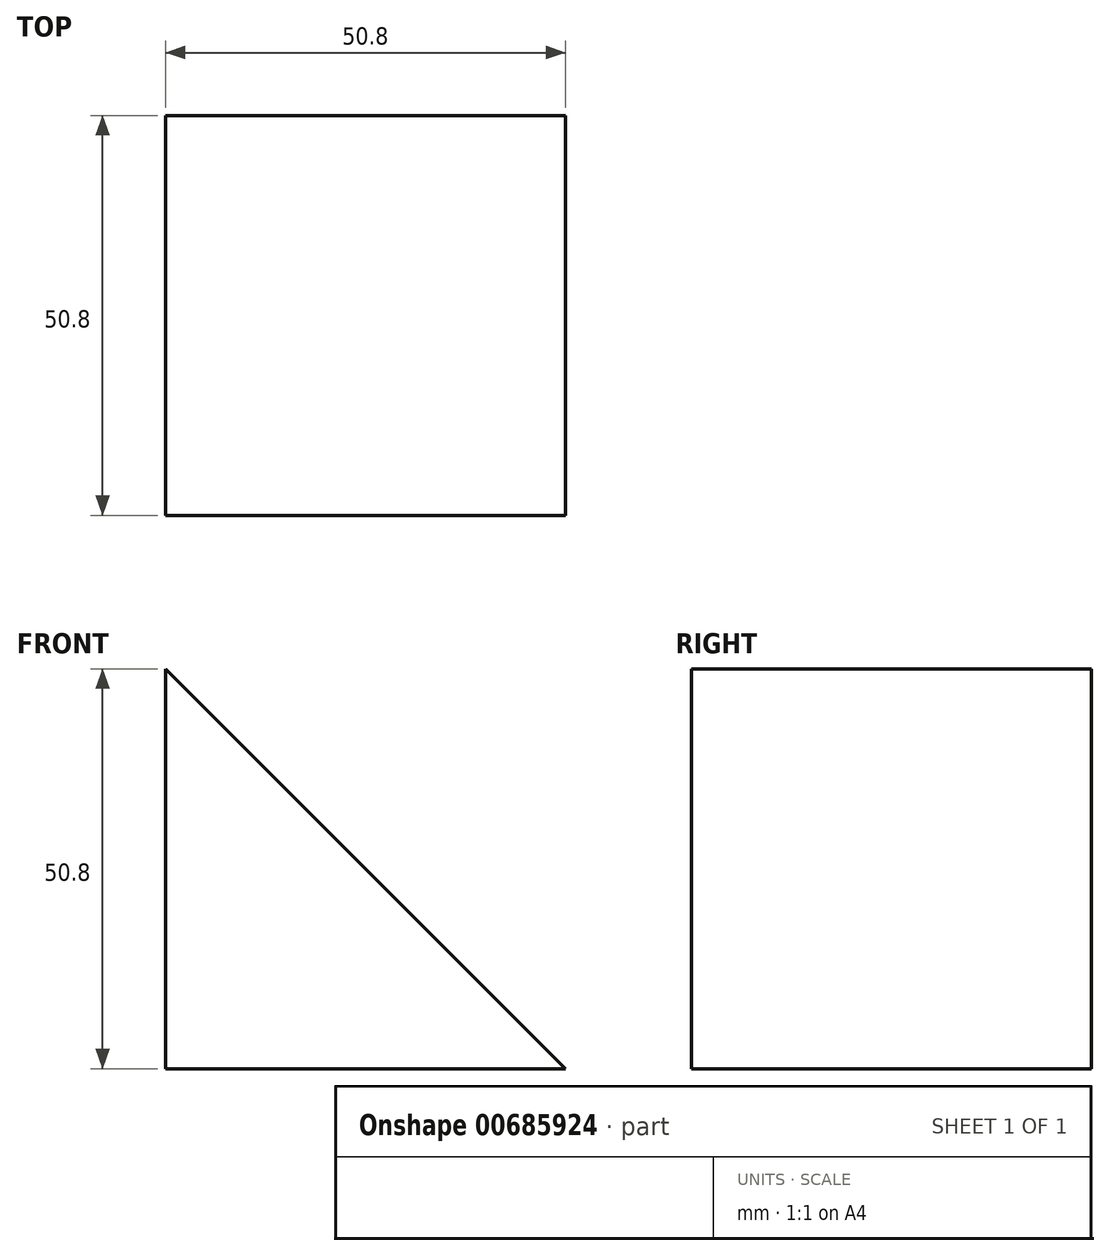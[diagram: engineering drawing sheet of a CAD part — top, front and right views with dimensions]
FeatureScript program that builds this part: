
annotation { "Feature Type Name" : "Feature", "Feature Type Description" : "" }
export const myFeature = defineFeature(function(context is Context, id is Id, definition is map)
    precondition{}
    {
        {
            var Q0;
            Q0=qCreatedBy(makeId("Front.planeOp"),FACE);
            var sketch = newSketch(context, id + "F0", { "sketchPlane" : qUnion([Q0])});
            skLineSegment(sketch, "E0", {"start": v(0, 0) * mm, "end": v(0, 50.8) * mm});
            skLineSegment(sketch, "E1", {"start": v(0, 0) * mm, "end": v(50.8, 0) * mm});
            skLineSegment(sketch, "E2", {"start": v(0, 50.8) * mm, "end": v(50.8, 0) * mm});
            skSolve(sketch);
        }
        {
            var Q0;
            Q0 = qSketchRegion(id + "F0", true);
            extrude(context, id + "F1", {"entities" : qUnion([Q0]), "depth" : 50.8 * mm, "offsetDistance" : 25.4 * mm});
        }
    });
